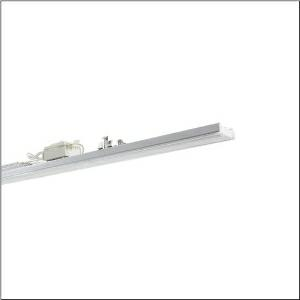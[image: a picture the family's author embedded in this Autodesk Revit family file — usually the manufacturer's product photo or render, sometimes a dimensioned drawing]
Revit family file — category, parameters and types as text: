
# Revit family: licross_r__11_recessed_ho_51te12dn4exm3s4_3c59
name_source: partatom
category: Lighting Fixtures
units: mm (PartAtom-declared; Revit-internal decimal feet)

## family parameters
Cut with Voids When Loaded = No
Host = Face
Light Source = No
Part Type = Normal
Room Calculation Point = No
Round Connector Dimension = Use Diameter
Shared = No

## types (1)
- --- (1 x LED, 1000 lm, 7.2 W, 4000K)
    Apparent Load = 7 VA
    CIE Flux Codes = 66 91 98 100 100
    Color Rendering = 80
    Color Temperature = 4000K
    Default Elevation = 1800 mm
    Description = Licross® 11 Recessed HO, luminaire insert, of sheet steel, galvanised, coil coated, white, length: 1.500mm, width: 66mm, height: 67mm, LED rated luminous flux: 14.030lm, light colour: 840, control gear: DALI 2, with plug, 6-pole, with phase selection, for trunking rail, 9 or 11-core, mains connection: 220..240V, AC, 50/60Hz, rated input power: 81W, for trunking rail, 9-/11-core, internal wiring halogen-free, for emergency light function, converter,control gear: single battery element, battery: LiFePO4, 9Ah, primary optical cover: cover, of PMMA, light emission: direct distribution, primary light characteristic: symmetric, protection rating (complete): IP54, insulation class (complete): insulation class I (protective earthing), certification: CE, UKCA, protection symbol: D if used in an environment with non-conductive dust loads with corresponding accessories, impact resistance: IK06, permissible ambient temperature for indoor applications: +5..+30°C, standard: EN 60598-2-22, LABS conformity tested according to VDMA 24364:2018-05, reducing of maximum allowable ambient temperature of 5°C with ceiling mounting, corresponds to IFS (International Featured Standards) requirements for safety and quality in the food industry, packaging unit: 1 piece
    Height = 58 mm
    Lamp = 1 x LED
    Lamp Light Flux = 1000 lm
    Lamp Power = 7.2 W
    Lamp count = 1
    Length = 1500 mm
    Luminous efficacy = 139 lm/W
    Manufacturer = Siteco
    ModVariant = No
    Model = 51TE12DN4EXM3S4
    Mounting Place = Ceiling
    Mounting Type = Pendant
    Number of Poles = 1
    OnlyDefault = Yes
    Power Factor = 1
    Product Name = Licross® 11 Recessed HO
    Product group = luminaire insert | ceiling pendant
    ProductGroupID = 902
    Protection Class = Protection class I
    Protection Degree = IP 54
    RLX_Detail_Level = 1
    RLX_Emergency_Light_Flux = 0 lm
    RLX_Emergency_Type = 0
    RLX_Emergency_Type_DB = No
    RlxData = <blob elided: 24993 chars, md5=5cc1d703>
    Socket = socket
    Standby Power = 0 W
    System Light Flux = 1000 lm
    System Power = 7 W
    Type Comments = : emergency light operation: 3 h
    Type Image = l_1296930.jpg
    URL = http://relux.com
    VarID = @adj_111417
    Voltage = 0 V
    Weight = 0.00 kg
    Width = 66 mm

## geometry (parser evidence)
native form markers: Blend x4, Sweep x10
no freeform markers — native parametric forms only
